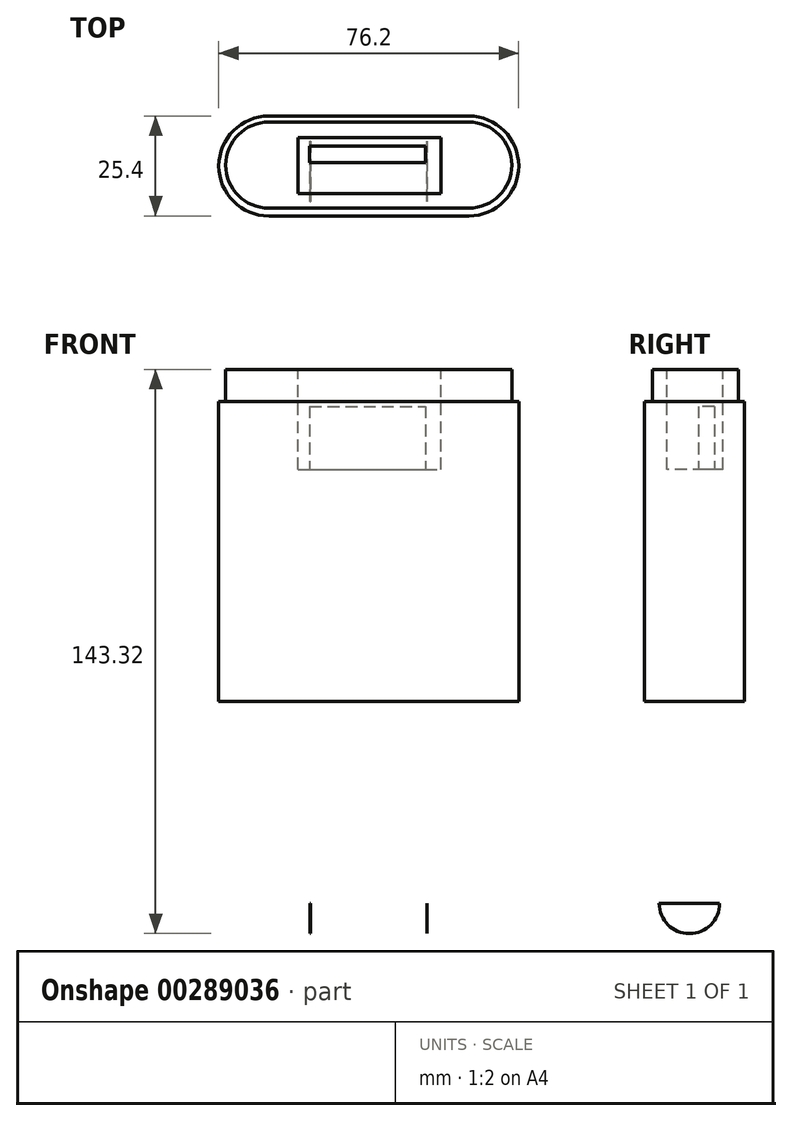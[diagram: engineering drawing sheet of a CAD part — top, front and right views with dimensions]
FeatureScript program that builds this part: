
annotation { "Feature Type Name" : "Feature", "Feature Type Description" : "" }
export const myFeature = defineFeature(function(context is Context, id is Id, definition is map)
    precondition{}
    {
        {
            var Q0;
            Q0=qCreatedBy(makeId("Top.planeOp"),FACE);
            var sketch = newSketch(context, id + "F0", { "sketchPlane" : qUnion([Q0])});
            skLineSegment(sketch, "E0.bottom", {"start": v(-30, 15.33) * mm, "end": v(20.8, 15.33) * mm});
            skLineSegment(sketch, "E0.top", {"start": v(-30, -10.07) * mm, "end": v(20.8, -10.07) * mm});
            skLineSegment(sketch, "E0.left", {"start": v(-30, 15.33) * mm, "end": v(-30, -10.07) * mm});
            skLineSegment(sketch, "E0.right", {"start": v(20.8, 15.33) * mm, "end": v(20.8, -10.07) * mm});
            skArc(sketch, "E1", {"start": v(20.8, -10.07) * mm, "mid": v(33.5, 2.63) * mm, "end": v(20.8, 15.33) * mm});
            skArc(sketch, "E2", {"start": v(-30, 15.33) * mm, "mid": v(-42.7, 2.63) * mm, "end": v(-30, -10.07) * mm});
            skSolve(sketch);
        }
        {
            var Q0;
            Q0 = qSketchRegion(id + "F0", true);
            var Q1;
            Q1=makeQuery(id+"F0.imprint","IMPRINT",FACE,{"disambiguationData":[TD([[makeQuery(id+"F0.imprint","IMPRINT",EDGE,{"derivedFrom":sQuery(id+"F0.wireOp",EDGE,"E0.bottom")}),-1.0]])]});
            extrude(context, id + "F1", {"entities" : qUnion([Q0, Q1]), "depth" : 76.2 * mm});
        }
        {
            var Q0;
            Q0=makeQuery(id+"F1.opExtrude","CAP_FACE",FACE,{"disambiguationData":[OSD([sQuery(id+"F0.wireOp",EDGE,"E0.bottom"),sQuery(id+"F0.wireOp",EDGE,"E0.top"),sQuery(id+"F0.wireOp",EDGE,"E1"),sQuery(id+"F0.wireOp",EDGE,"E2")])],"isStart":false});
            var sketch = newSketch(context, id + "F2", { "sketchPlane" : qUnion([Q0])});
            skLineSegment(sketch, "E3.bottom", {"start": v(-30, 13.77) * mm, "end": v(20.8, 13.77) * mm});
            skLineSegment(sketch, "E3.top", {"start": v(-30, -8.1) * mm, "end": v(20.8, -8.1) * mm});
            skLineSegment(sketch, "E3.left", {"start": v(-30, 13.77) * mm, "end": v(-30, -8.1) * mm});
            skLineSegment(sketch, "E3.right", {"start": v(20.8, 13.77) * mm, "end": v(20.8, -8.1) * mm});
            skArc(sketch, "E4", {"start": v(20.8, -8.1) * mm, "mid": v(31.73, 2.83) * mm, "end": v(20.8, 13.77) * mm});
            skArc(sketch, "E5", {"start": v(-30, 13.77) * mm, "mid": v(-40.94, 2.83) * mm, "end": v(-30, -8.1) * mm});
            skSolve(sketch);
        }
        {
            var Q0;
            Q0=makeQuery(id+"F2.imprint","IMPRINT",FACE,{"disambiguationData":[TD([[makeQuery(id+"F2.imprint","IMPRINT",EDGE,{"derivedFrom":sQuery(id+"F2.wireOp",EDGE,"E3.right")}),1.0]])]});
            var Q1;
            Q1=makeQuery(id+"F2.imprint","IMPRINT",FACE,{"disambiguationData":[TD([[makeQuery(id+"F2.imprint","IMPRINT",EDGE,{"derivedFrom":sQuery(id+"F2.wireOp",EDGE,"E3.bottom")}),-1.0]])]});
            var Q2;
            Q2=makeQuery(id+"F2.imprint","IMPRINT",FACE,{"disambiguationData":[TD([[makeQuery(id+"F2.imprint","IMPRINT",EDGE,{"derivedFrom":sQuery(id+"F2.wireOp",EDGE,"E3.left")}),-1.0]])]});
            extrude(context, id + "F3", {"entities" : qUnion([Q0, Q1, Q2]), "operationType" : NewBodyOperationType.ADD, "depth" : 8.13 * mm});
        }
        {
            var Q0;
            Q0=makeQuery(id+"F3.opExtrude","CAP_FACE",FACE,{"disambiguationData":[OSD([sQuery(id+"F2.wireOp",EDGE,"E3.bottom"),sQuery(id+"F2.wireOp",EDGE,"E3.top"),sQuery(id+"F2.wireOp",EDGE,"E4"),sQuery(id+"F2.wireOp",EDGE,"E5")])],"isStart":false});
            var sketch = newSketch(context, id + "F4", { "sketchPlane" : qUnion([Q0])});
            skLineSegment(sketch, "E6.bottom", {"start": v(-22.53, 9.86) * mm, "end": v(13.8, 9.86) * mm});
            skLineSegment(sketch, "E6.top", {"start": v(-22.53, -4.35) * mm, "end": v(13.8, -4.35) * mm});
            skLineSegment(sketch, "E6.left", {"start": v(-22.53, 9.86) * mm, "end": v(-22.53, -4.35) * mm});
            skLineSegment(sketch, "E6.right", {"start": v(13.8, 9.86) * mm, "end": v(13.8, -4.35) * mm});
            skSolve(sketch);
        }
        {
            var Q0;
            Q0 = qSketchRegion(id + "F4", true);
            extrude(context, id + "F5", {"entities" : qUnion([Q0]), "operationType" : NewBodyOperationType.REMOVE, "oppositeDirection" : true, "depth" : 25.4 * mm});
        }
        {
            var Q0;
            Q0=makeQuery(id+"F5.boolean.opBoolean","COPY",FACE,{"derivedFrom":makeQuery(id+"F5.opExtrude","CAP_FACE",FACE,{"disambiguationData":[OSD([sQuery(id+"F4.wireOp",EDGE,"E6.bottom"),sQuery(id+"F4.wireOp",EDGE,"E6.top"),sQuery(id+"F4.wireOp",EDGE,"E6.left"),sQuery(id+"F4.wireOp",EDGE,"E6.right")])],"isStart":false})});
            var sketch = newSketch(context, id + "F6", { "sketchPlane" : qUnion([Q0])});
            skLineSegment(sketch, "E7.bottom", {"start": v(-19.67, 7.64) * mm, "end": v(9.83, 7.64) * mm});
            skLineSegment(sketch, "E7.top", {"start": v(-19.67, 3.54) * mm, "end": v(9.83, 3.54) * mm});
            skLineSegment(sketch, "E7.left", {"start": v(-19.67, 7.64) * mm, "end": v(-19.67, 3.54) * mm});
            skLineSegment(sketch, "E7.right", {"start": v(9.83, 7.64) * mm, "end": v(9.83, 3.54) * mm});
            skSolve(sketch);
        }
        {
            var Q0;
            Q0 = qSketchRegion(id + "F6", true);
            extrude(context, id + "F7", {"entities" : qUnion([Q0]), "operationType" : NewBodyOperationType.ADD, "depth" : 16 * mm});
        }
        {
            var Q0;
            Q0=makeQuery(id+"F1.opExtrude","CAP_FACE",FACE,{"disambiguationData":[OSD([sQuery(id+"F0.wireOp",EDGE,"E0.bottom"),sQuery(id+"F0.wireOp",EDGE,"E0.top"),sQuery(id+"F0.wireOp",EDGE,"E1"),sQuery(id+"F0.wireOp",EDGE,"E2")])],"isStart":true});
            var sketch = newSketch(context, id + "F8", { "sketchPlane" : qUnion([Q0])});
            skLineSegment(sketch, "E8", {"start": v(-4.6, 10.07) * mm, "end": v(-4.6, -15.33) * mm});
            skLineSegment(sketch, "E9", {"start": v(10.24, 6.39) * mm, "end": v(10.24, -8.98) * mm});
            skLineSegment(sketch, "E10.MirrorCS", {"start": v(-19.45, 6.39) * mm, "end": v(-19.45, -8.98) * mm});
            skSolve(sketch);
        }
        {
            var Q0;
            Q0=sQuery(id+"F8.wireOp",EDGE,"E10.MirrorCS");
            var Q1;
            Q1=sQuery(id+"F8.wireOp",EDGE,"E9");
            extrude(context, id + "F9", {"bodyType" : ToolBodyType.SURFACE, "surfaceEntities" : qUnion([Q0, Q1]), "depth" : 51.3 * mm});
        }
        {
            var Q0;
            Q0=makeQuery(id+"F9.opExtrude","SWEPT_FACE",FACE,{"disambiguationData":[OSD([sQuery(id+"F8.wireOp",EDGE,"E10.MirrorCS")])]});
            var sketch = newSketch(context, id + "F10", { "sketchPlane" : qUnion([Q0])});
            skArc(sketch, "E11", {"start": v(-8.98, -51.3) * mm, "mid": v(-1.3, -59) * mm, "end": v(6.39, -51.3) * mm});
            skSolve(sketch);
        }
        {
            var Q0;
            Q0 = qSketchRegion(id + "F10", true);
            var Q1;
            Q1=makeQuery(id+"F10.imprint","IMPRINT",FACE,{"disambiguationData":[TD([[makeQuery(id+"F10.imprint","IMPRINT",EDGE,{"derivedFrom":sQuery(id+"F10.wireOp",EDGE,"E11")}),1.0]])]});
            extrude(context, id + "F11", {"entities" : qUnion([Q0, Q1]), "depth" : 0.03 * mm});
        }
        {
            var Q0;
            Q0=makeQuery(id+"F9.opExtrude","SWEPT_FACE",FACE,{"disambiguationData":[OSD([sQuery(id+"F8.wireOp",EDGE,"E9")])]});
            var sketch = newSketch(context, id + "F12", { "sketchPlane" : qUnion([Q0])});
            skArc(sketch, "E12", {"start": v(-8.98, -51.3) * mm, "mid": v(-1.3, -59) * mm, "end": v(6.39, -51.3) * mm});
            skSolve(sketch);
        }
        {
            var Q0;
            Q0 = qSketchRegion(id + "F12", true);
            var Q1;
            Q1=makeQuery(id+"F12.imprint","IMPRINT",FACE,{"disambiguationData":[TD([[makeQuery(id+"F12.imprint","IMPRINT",EDGE,{"derivedFrom":sQuery(id+"F12.wireOp",EDGE,"E12")}),1.0]])]});
            extrude(context, id + "F13", {"entities" : qUnion([Q0, Q1]), "depth" : 0.03 * mm});
        }
    });
